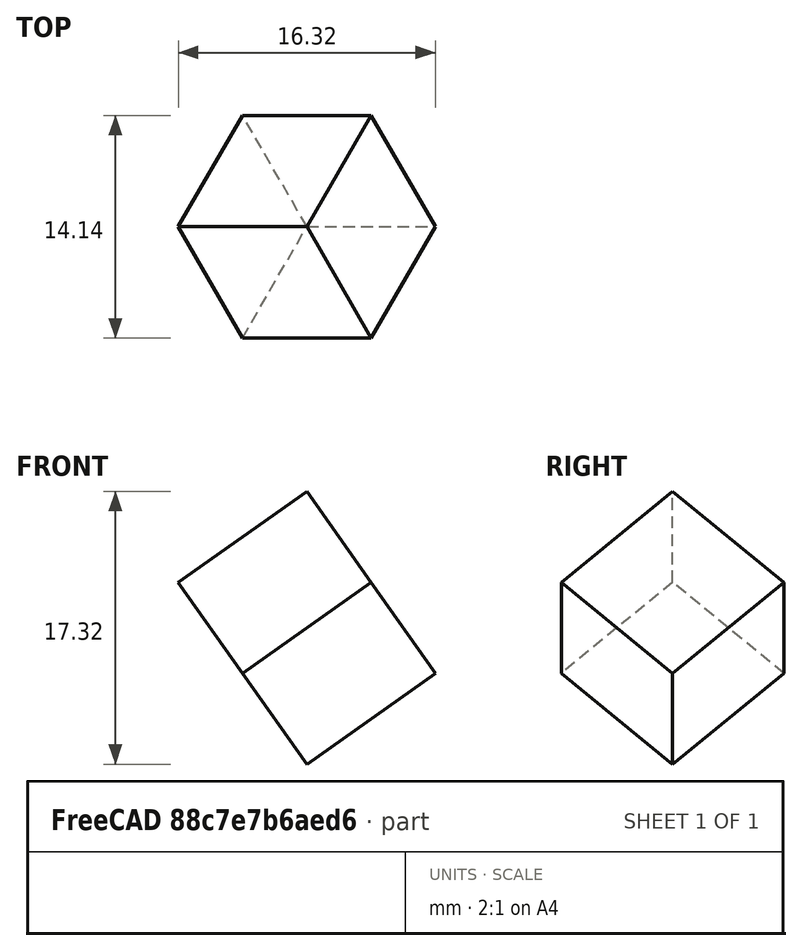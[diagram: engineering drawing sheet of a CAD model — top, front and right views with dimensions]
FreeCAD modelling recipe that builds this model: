
FCSTD DOCUMENT  (FreeCAD 0.19R17089 +1543 (Git))
Label: cube-on-corner-001
License: All rights reserved
LicenseURL: http://en.wikipedia.org/wiki/All_rights_reserved
objects: Sketcher::SketchObject×3, App::DocumentObjectGroup×1, PartDesign::Pad×1, PartDesign::Body×1
note: 6 computed .brp shape members not serialized (recipe doc carries the construction recipe); baked Part::Feature solids carry a one-line shape summary decoded from their .brp

FEATURE [Sketcher::SketchObject] Sketch
  Placement = pos=(0,0,0) rot=(1,0,0;1.5708rad)
  sketch-geometry (3):
    g0: LineSegment StartX=0 StartY=-9e-16 StartZ=0 EndX=7 EndY=0 EndZ=0
    g1: LineSegment StartX=7 StartY=0 StartZ=0 EndX=7 EndY=5 EndZ=0
    g2: LineSegment StartX=7 StartY=5 StartZ=0 EndX=0 EndY=-9e-16 EndZ=0
  constraints (10):
    c: Coincident(g-1,g0)
    c: PointOnObject(g0,g-1)
    c: Coincident(g0,g1)
    c: Vertical(g1)
    c: Coincident(g1,g2)
    c: Coincident(g2,g0)
    c: Distance(g1) = 5  'HSL'
    c: Distance(g0) = 7  'HCDL'
    c: Angle(g0,g2) = 0.620249
    c: Angle(g2,g-2) = 0.950547
FEATURE [Sketcher::SketchObject] Sketch001
  Placement = pos=(0,0,0) rot=(1,0,0;1.5708rad)
  expr: Constraints[2] = Sketch.Constraints.HCDL * 2 + 15mm
  sketch-geometry (1):
    g0: LineSegment StartX=0 StartY=14.5 StartZ=0 EndX=0 EndY=-14.5 EndZ=0
  constraints (3):
    c: PointOnObject(g0,g-2)
    c: Symmetric(g0,g0,g-1)
    c: DistanceY(g0,g0) = 29
FEATURE [App::DocumentObjectGroup] Group  label="Repository"
  Group = -> [Sketch,Sketch001]
FEATURE [Sketcher::SketchObject] Sketch002
  MapMode = 5
  Support = -> [XY_Plane]
  expr: .Constraints.SL = Sketch.Constraints.HSL * 2
  sketch-geometry (5):
    g0: LineSegment StartX=7.07107 StartY=-9e-16 StartZ=0 EndX=-1.0694e-12 EndY=7.07107 EndZ=0
    g1: LineSegment StartX=-1.0694e-12 StartY=7.07107 StartZ=0 EndX=-7.07107 EndY=-3.633e-13 EndZ=0
    g2: LineSegment StartX=-7.07107 StartY=-3.633e-13 StartZ=0 EndX=6.48e-14 EndY=-7.07107 EndZ=0
    g3: LineSegment StartX=6.48e-14 StartY=-7.07107 StartZ=0 EndX=7.07107 EndY=-9e-16 EndZ=0
    g4: Circle [constr] CenterX=0 CenterY=0 CenterZ=0 NormalX=0 NormalY=0 NormalZ=1 AngleXU=0 Radius=7.07107
  constraints (14):
    c: Coincident(g0,g1)
    c: Coincident(g1,g2)
    c: Coincident(g2,g3)
    c: Coincident(g3,g0)
    c: Equal(g0,g1)
    c: Equal(g0,g2)
    c: Equal(g0,g3)
    c: PointOnObject(g0,g4)
    c: PointOnObject(g1,g4)
    c: PointOnObject(g2,g4)
    c: PointOnObject(g3,g4)
    c: Coincident(g4,g-1)
    c: PointOnObject(g3,g-1)
    c: Distance(g0) = 10  'SL'
FEATURE [PartDesign::Pad] Pad
  ClaimChildren = false
  Length = 10
  Length2 = 100
  Midplane = true
  Profile = -> Sketch002
  Type = 0
  expr: Length = Sketch.Constraints.HSL * 2
FEATURE [PartDesign::Body] Body
  Group = -> [Sketch002,Pad]
  Origin = -> Origin
  Placement = pos=(0,0,0) rot=(0,1,0;0.955317rad)
  Tip = -> Pad
  expr: .Placement.Rotation.Angle = 90deg - atan(sqrt(1 / 2))
